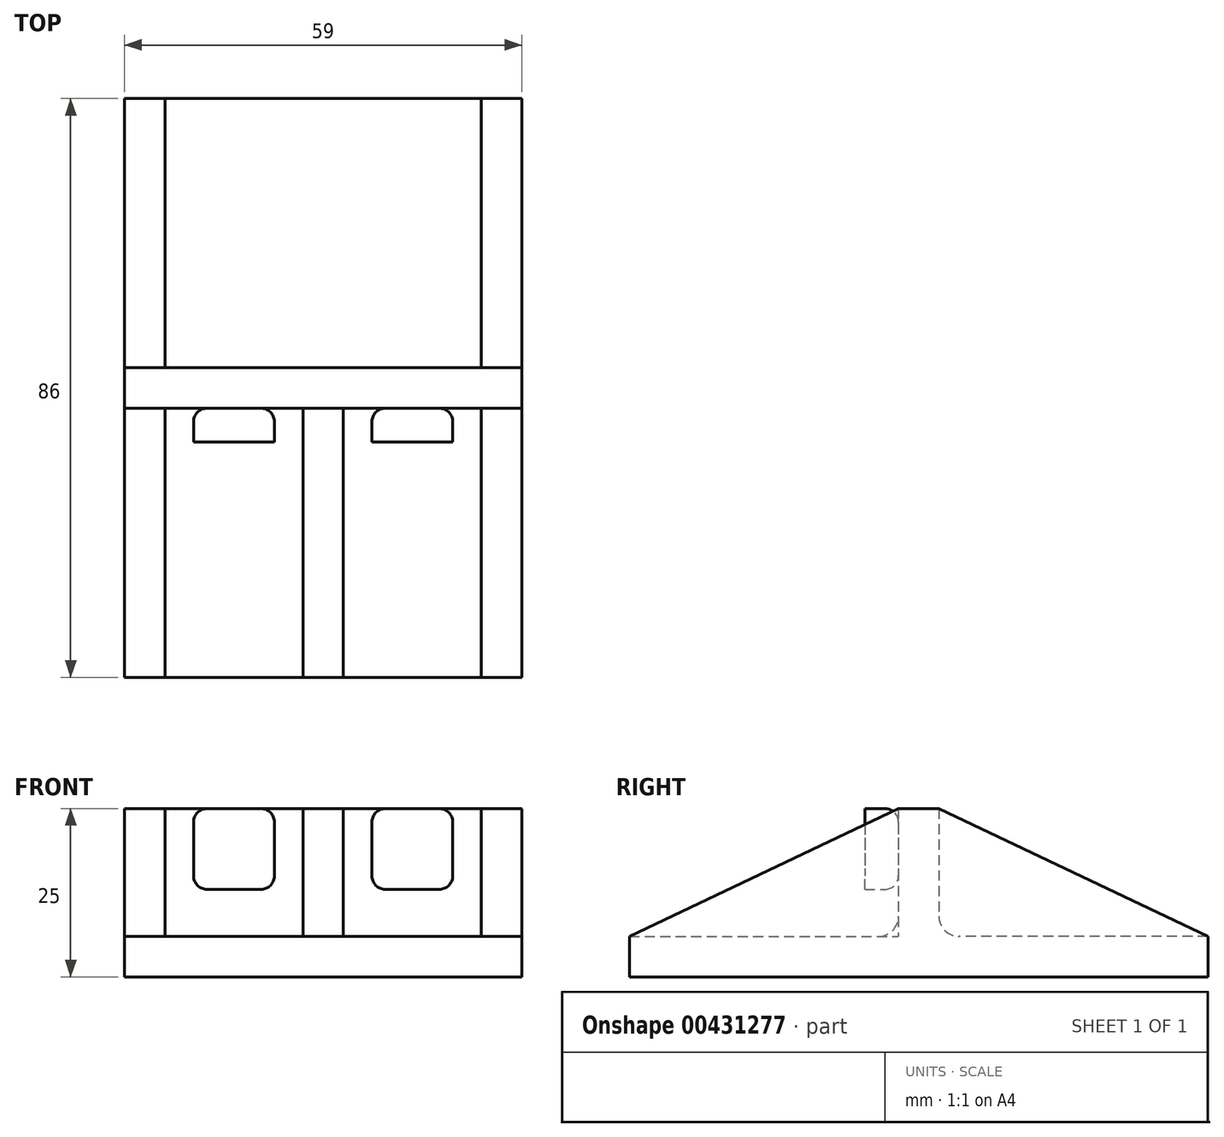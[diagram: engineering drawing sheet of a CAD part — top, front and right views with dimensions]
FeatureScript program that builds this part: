
annotation { "Feature Type Name" : "Feature", "Feature Type Description" : "" }
export const myFeature = defineFeature(function(context is Context, id is Id, definition is map)
    precondition{}
    {
        {
            var Q0;
            Q0=qCreatedBy(makeId("Top.planeOp"),FACE);
            var sketch = newSketch(context, id + "F0", { "sketchPlane" : qUnion([Q0])});
            skLineSegment(sketch, "E0.bottom", {"start": v(-29.5, 43) * mm, "end": v(29.5, 43) * mm});
            skLineSegment(sketch, "E0.top", {"start": v(-29.5, -43) * mm, "end": v(29.5, -43) * mm});
            skLineSegment(sketch, "E0.left", {"start": v(-29.5, 43) * mm, "end": v(-29.5, -43) * mm});
            skLineSegment(sketch, "E0.right", {"start": v(29.5, 43) * mm, "end": v(29.5, -43) * mm});
            skSolve(sketch);
        }
        {
            var Q0;
            Q0=makeQuery(id+"F0.imprint","IMPRINT",FACE,{"disambiguationData":[TD([[makeQuery(id+"F0.imprint","IMPRINT",EDGE,{"derivedFrom":sQuery(id+"F0.wireOp",EDGE,"E0.bottom")}),-1.0]])]});
            extrude(context, id + "F1", {"entities" : qUnion([Q0]), "depth" : 6 * mm});
        }
        {
            var Q0;
            Q0=makeQuery(id+"F1.opExtrude","CAP_FACE",FACE,{"disambiguationData":[OSD([sQuery(id+"F0.wireOp",EDGE,"E0.bottom"),sQuery(id+"F0.wireOp",EDGE,"E0.top"),sQuery(id+"F0.wireOp",EDGE,"E0.left"),sQuery(id+"F0.wireOp",EDGE,"E0.right")])],"isStart":false});
            var sketch = newSketch(context, id + "F2", { "sketchPlane" : qUnion([Q0])});
            skLineSegment(sketch, "E1.bottom", {"start": v(-29.5, 43) * mm, "end": v(-23.5, 43) * mm});
            skLineSegment(sketch, "E1.left", {"start": v(-29.5, 43) * mm, "end": v(-29.5, -43) * mm});
            skLineSegment(sketch, "E1.right", {"start": v(-23.5, 43) * mm, "end": v(-23.5, 3) * mm});
            skLineSegment(sketch, "E2.bottom", {"start": v(-23.5, 3) * mm, "end": v(23.5, 3) * mm});
            skLineSegment(sketch, "E2.top", {"start": v(-23.5, -3) * mm, "end": v(-3, -3) * mm});
            skLineSegment(sketch, "E2.right", {"start": v(29.5, 43) * mm, "end": v(29.5, -43) * mm});
            skLineSegment(sketch, "E3.bottom", {"start": v(-29.5, -43) * mm, "end": v(-23.5, -43) * mm});
            skLineSegment(sketch, "E3.right", {"start": v(-23.5, -43) * mm, "end": v(-23.5, -3) * mm});
            skLineSegment(sketch, "E4.bottom", {"start": v(29.5, -43) * mm, "end": v(23.5, -43) * mm});
            skLineSegment(sketch, "E4.right", {"start": v(23.5, -43) * mm, "end": v(23.5, -3) * mm});
            skLineSegment(sketch, "E5.bottom", {"start": v(29.5, 43) * mm, "end": v(23.5, 43) * mm});
            skLineSegment(sketch, "E5.right", {"start": v(23.5, 43) * mm, "end": v(23.5, 3) * mm});
            skLineSegment(sketch, "E6.bottom", {"start": v(3, -43) * mm, "end": v(-3, -43) * mm});
            skLineSegment(sketch, "E6.left", {"start": v(3, -43) * mm, "end": v(3, -3) * mm});
            skLineSegment(sketch, "E6.right", {"start": v(-3, -43) * mm, "end": v(-3, -3) * mm});
            skLineSegment(sketch, "E7.trimOffspring", {"start": v(3, -3) * mm, "end": v(23.5, -3) * mm});
            skPoint(sketch, "E8.orphan", {"position": v(29.5, -3) * mm});
            skSolve(sketch);
        }
        {
            var Q0;
            Q0=makeQuery(id+"F2.imprint","IMPRINT",FACE,{"disambiguationData":[TD([[makeQuery(id+"F2.imprint","IMPRINT",EDGE,{"derivedFrom":sQuery(id+"F2.wireOp",EDGE,"E1.bottom")}),-1.0]])]});
            extrude(context, id + "F3", {"entities" : qUnion([Q0]), "operationType" : NewBodyOperationType.ADD, "depth" : 19 * mm});
        }
        {
            var Q0;
            Q0=makeQuery(id+"F3.boolean.opBoolean","MERGE",FACE,{"derivedFrom":[makeQuery(id+"F1.opExtrude","SWEPT_FACE",FACE,{"disambiguationData":[OSD([sQuery(id+"F0.wireOp",EDGE,"E0.right")])]}),makeQuery(id+"F3.opExtrude","SWEPT_FACE",FACE,{"disambiguationData":[OSD([sQuery(id+"F2.wireOp",EDGE,"E2.right")])]})]});
            var sketch = newSketch(context, id + "F4", { "sketchPlane" : qUnion([Q0])});
            skLineSegment(sketch, "E9", {"start": v(-43, 6) * mm, "end": v(-3, 25) * mm});
            skLineSegment(sketch, "E10", {"start": v(-3, 25) * mm, "end": v(-43, 25) * mm});
            skLineSegment(sketch, "E11", {"start": v(-43, 25) * mm, "end": v(-43, 6) * mm});
            skLineSegment(sketch, "E12", {"start": v(43, 6) * mm, "end": v(3, 25) * mm});
            skLineSegment(sketch, "E13", {"start": v(3, 25) * mm, "end": v(43, 25) * mm});
            skLineSegment(sketch, "E14", {"start": v(43, 25) * mm, "end": v(43, 6) * mm});
            skSolve(sketch);
        }
        {
            var Q0;
            Q0=makeQuery(id+"F4.imprint","IMPRINT",FACE,{"disambiguationData":[TD([[makeQuery(id+"F4.imprint","IMPRINT",EDGE,{"derivedFrom":sQuery(id+"F4.wireOp",EDGE,"E9")}),1.0]])]});
            var Q1;
            Q1=makeQuery(id+"F4.imprint","IMPRINT",FACE,{"disambiguationData":[TD([[makeQuery(id+"F4.imprint","IMPRINT",EDGE,{"derivedFrom":sQuery(id+"F4.wireOp",EDGE,"E12")}),-1.0]])]});
            extrude(context, id + "F5", {"entities" : qUnion([Q0, Q1]), "operationType" : NewBodyOperationType.REMOVE, "endBound" : BoundingType.THROUGH_ALL, "oppositeDirection" : true, "depth" : 25 * mm});
        }
        {
            var Q0;
            Q0=makeQuery(id+"F3.opExtrude","SWEPT_FACE",FACE,{"disambiguationData":[OSD([sQuery(id+"F2.wireOp",EDGE,"E2.top")])]});
            var sketch = newSketch(context, id + "F6", { "sketchPlane" : qUnion([Q0])});
            skLineSegment(sketch, "E15.bottom", {"start": v(-19.25, 25) * mm, "end": v(-7.25, 25) * mm});
            skLineSegment(sketch, "E15.top", {"start": v(-19.25, 13) * mm, "end": v(-7.25, 13) * mm});
            skLineSegment(sketch, "E15.left", {"start": v(-19.25, 25) * mm, "end": v(-19.25, 13) * mm});
            skLineSegment(sketch, "E15.right", {"start": v(-7.25, 25) * mm, "end": v(-7.25, 13) * mm});
            skLineSegment(sketch, "E16.bottom", {"start": v(7.25, 25) * mm, "end": v(19.25, 25) * mm});
            skLineSegment(sketch, "E16.top", {"start": v(7.25, 13) * mm, "end": v(19.25, 13) * mm});
            skLineSegment(sketch, "E16.left", {"start": v(7.25, 25) * mm, "end": v(7.25, 13) * mm});
            skLineSegment(sketch, "E16.right", {"start": v(19.25, 25) * mm, "end": v(19.25, 13) * mm});
            skSolve(sketch);
        }
        {
            var Q0;
            Q0=makeQuery(id+"F3.opExtrude","CAP_EDGE",EDGE,{"disambiguationData":[OSD([sQuery(id+"F2.wireOp",EDGE,"E2.top")])],"isStart":true});
            var Q1;
            Q1=makeQuery(id+"F3.opExtrude","CAP_EDGE",EDGE,{"disambiguationData":[OSD([sQuery(id+"F2.wireOp",EDGE,"E7.trimOffspring")])],"isStart":true});
            var Q2;
            Q2=makeQuery(id+"F3.opExtrude","CAP_EDGE",EDGE,{"disambiguationData":[OSD([sQuery(id+"F2.wireOp",EDGE,"E2.bottom")])],"isStart":true});
            fillet(context, id + "F7", {"entities" : qUnion([Q0, Q1, Q2]), "radius" : 3 * mm, "tangentPropagation" : true, "allowEdgeOverflow" : false});
        }
        {
            var Q0;
            Q0=makeQuery(id+"F6.imprint","IMPRINT",FACE,{"disambiguationData":[TD([[makeQuery(id+"F6.imprint","IMPRINT",EDGE,{"derivedFrom":sQuery(id+"F6.wireOp",EDGE,"E15.bottom")}),-1.0]])]});
            var Q1;
            Q1=makeQuery(id+"F6.imprint","IMPRINT",FACE,{"disambiguationData":[TD([[makeQuery(id+"F6.imprint","IMPRINT",EDGE,{"derivedFrom":sQuery(id+"F6.wireOp",EDGE,"E16.bottom")}),-1.0]])]});
            extrude(context, id + "F8", {"entities" : qUnion([Q0, Q1]), "depth" : 5 * mm});
        }
        {
            var Q0;
            Q0=makeQuery(id+"F8.opExtrude","CAP_EDGE",EDGE,{"disambiguationData":[OSD([sQuery(id+"F6.wireOp",EDGE,"E15.right")])],"isStart":true});
            var Q1;
            Q1=makeQuery(id+"F8.opExtrude","CAP_EDGE",EDGE,{"disambiguationData":[OSD([sQuery(id+"F6.wireOp",EDGE,"E15.bottom")])],"isStart":true});
            var Q2;
            Q2=makeQuery(id+"F8.opExtrude","CAP_EDGE",EDGE,{"disambiguationData":[OSD([sQuery(id+"F6.wireOp",EDGE,"E15.left")])],"isStart":true});
            var Q3;
            Q3=makeQuery(id+"F8.opExtrude","CAP_EDGE",EDGE,{"disambiguationData":[OSD([sQuery(id+"F6.wireOp",EDGE,"E15.top")])],"isStart":true});
            var Q4;
            Q4=makeQuery(id+"F8.opExtrude","CAP_EDGE",EDGE,{"disambiguationData":[OSD([sQuery(id+"F6.wireOp",EDGE,"E16.top")])],"isStart":true});
            var Q5;
            Q5=makeQuery(id+"F8.opExtrude","CAP_EDGE",EDGE,{"disambiguationData":[OSD([sQuery(id+"F6.wireOp",EDGE,"E16.left")])],"isStart":true});
            var Q6;
            Q6=makeQuery(id+"F8.opExtrude","CAP_EDGE",EDGE,{"disambiguationData":[OSD([sQuery(id+"F6.wireOp",EDGE,"E16.right")])],"isStart":true});
            var Q7;
            Q7=makeQuery(id+"F8.opExtrude","CAP_EDGE",EDGE,{"disambiguationData":[OSD([sQuery(id+"F6.wireOp",EDGE,"E16.bottom")])],"isStart":true});
            fillet(context, id + "F9", {"entities" : qUnion([Q0, Q1, Q2, Q3, Q4, Q5, Q6, Q7]), "radius" : 2 * mm, "tangentPropagation" : true, "allowEdgeOverflow" : false});
        }
        {
            var Q0;
            Q0=makeQuery(id+"F9.opFillet","BLEND_EDGE",EDGE,{"blendedFrom":[makeQuery(id+"F8.opExtrude","CAP_EDGE",EDGE,{"disambiguationData":[OSD([sQuery(id+"F6.wireOp",EDGE,"E15.bottom")])],"isStart":true}),makeQuery(id+"F8.opExtrude","CAP_EDGE",EDGE,{"disambiguationData":[OSD([sQuery(id+"F6.wireOp",EDGE,"E15.left")])],"isStart":true})],"blendedInto":[]});
            var Q1;
            Q1=makeQuery(id+"F9.opFillet","BLEND_EDGE",EDGE,{"blendedFrom":[makeQuery(id+"F8.opExtrude","CAP_EDGE",EDGE,{"disambiguationData":[OSD([sQuery(id+"F6.wireOp",EDGE,"E15.bottom")])],"isStart":true}),makeQuery(id+"F8.opExtrude","CAP_EDGE",EDGE,{"disambiguationData":[OSD([sQuery(id+"F6.wireOp",EDGE,"E15.right")])],"isStart":true})],"blendedInto":[]});
            var Q2;
            Q2=makeQuery(id+"F9.opFillet","BLEND_EDGE",EDGE,{"blendedFrom":[makeQuery(id+"F8.opExtrude","CAP_EDGE",EDGE,{"disambiguationData":[OSD([sQuery(id+"F6.wireOp",EDGE,"E15.top")])],"isStart":true}),makeQuery(id+"F8.opExtrude","CAP_EDGE",EDGE,{"disambiguationData":[OSD([sQuery(id+"F6.wireOp",EDGE,"E15.left")])],"isStart":true})],"blendedInto":[]});
            var Q3;
            Q3=makeQuery(id+"F9.opFillet","BLEND_EDGE",EDGE,{"blendedFrom":[makeQuery(id+"F8.opExtrude","CAP_EDGE",EDGE,{"disambiguationData":[OSD([sQuery(id+"F6.wireOp",EDGE,"E15.top")])],"isStart":true}),makeQuery(id+"F8.opExtrude","CAP_EDGE",EDGE,{"disambiguationData":[OSD([sQuery(id+"F6.wireOp",EDGE,"E15.right")])],"isStart":true})],"blendedInto":[]});
            var Q4;
            Q4=makeQuery(id+"F9.opFillet","BLEND_EDGE",EDGE,{"blendedFrom":[makeQuery(id+"F8.opExtrude","CAP_EDGE",EDGE,{"disambiguationData":[OSD([sQuery(id+"F6.wireOp",EDGE,"E16.bottom")])],"isStart":true}),makeQuery(id+"F8.opExtrude","CAP_EDGE",EDGE,{"disambiguationData":[OSD([sQuery(id+"F6.wireOp",EDGE,"E16.left")])],"isStart":true})],"blendedInto":[]});
            var Q5;
            Q5=makeQuery(id+"F9.opFillet","BLEND_EDGE",EDGE,{"blendedFrom":[makeQuery(id+"F8.opExtrude","CAP_EDGE",EDGE,{"disambiguationData":[OSD([sQuery(id+"F6.wireOp",EDGE,"E16.top")])],"isStart":true}),makeQuery(id+"F8.opExtrude","CAP_EDGE",EDGE,{"disambiguationData":[OSD([sQuery(id+"F6.wireOp",EDGE,"E16.left")])],"isStart":true})],"blendedInto":[]});
            var Q6;
            Q6=makeQuery(id+"F9.opFillet","BLEND_EDGE",EDGE,{"blendedFrom":[makeQuery(id+"F8.opExtrude","CAP_EDGE",EDGE,{"disambiguationData":[OSD([sQuery(id+"F6.wireOp",EDGE,"E16.bottom")])],"isStart":true}),makeQuery(id+"F8.opExtrude","CAP_EDGE",EDGE,{"disambiguationData":[OSD([sQuery(id+"F6.wireOp",EDGE,"E16.right")])],"isStart":true})],"blendedInto":[]});
            var Q7;
            Q7=makeQuery(id+"F9.opFillet","BLEND_EDGE",EDGE,{"blendedFrom":[makeQuery(id+"F8.opExtrude","CAP_EDGE",EDGE,{"disambiguationData":[OSD([sQuery(id+"F6.wireOp",EDGE,"E16.top")])],"isStart":true}),makeQuery(id+"F8.opExtrude","CAP_EDGE",EDGE,{"disambiguationData":[OSD([sQuery(id+"F6.wireOp",EDGE,"E16.right")])],"isStart":true})],"blendedInto":[]});
            fillet(context, id + "F10", {"entities" : qUnion([Q0, Q1, Q2, Q3, Q4, Q5, Q6, Q7]), "radius" : 2 * mm, "tangentPropagation" : true, "allowEdgeOverflow" : false});
        }
    });
